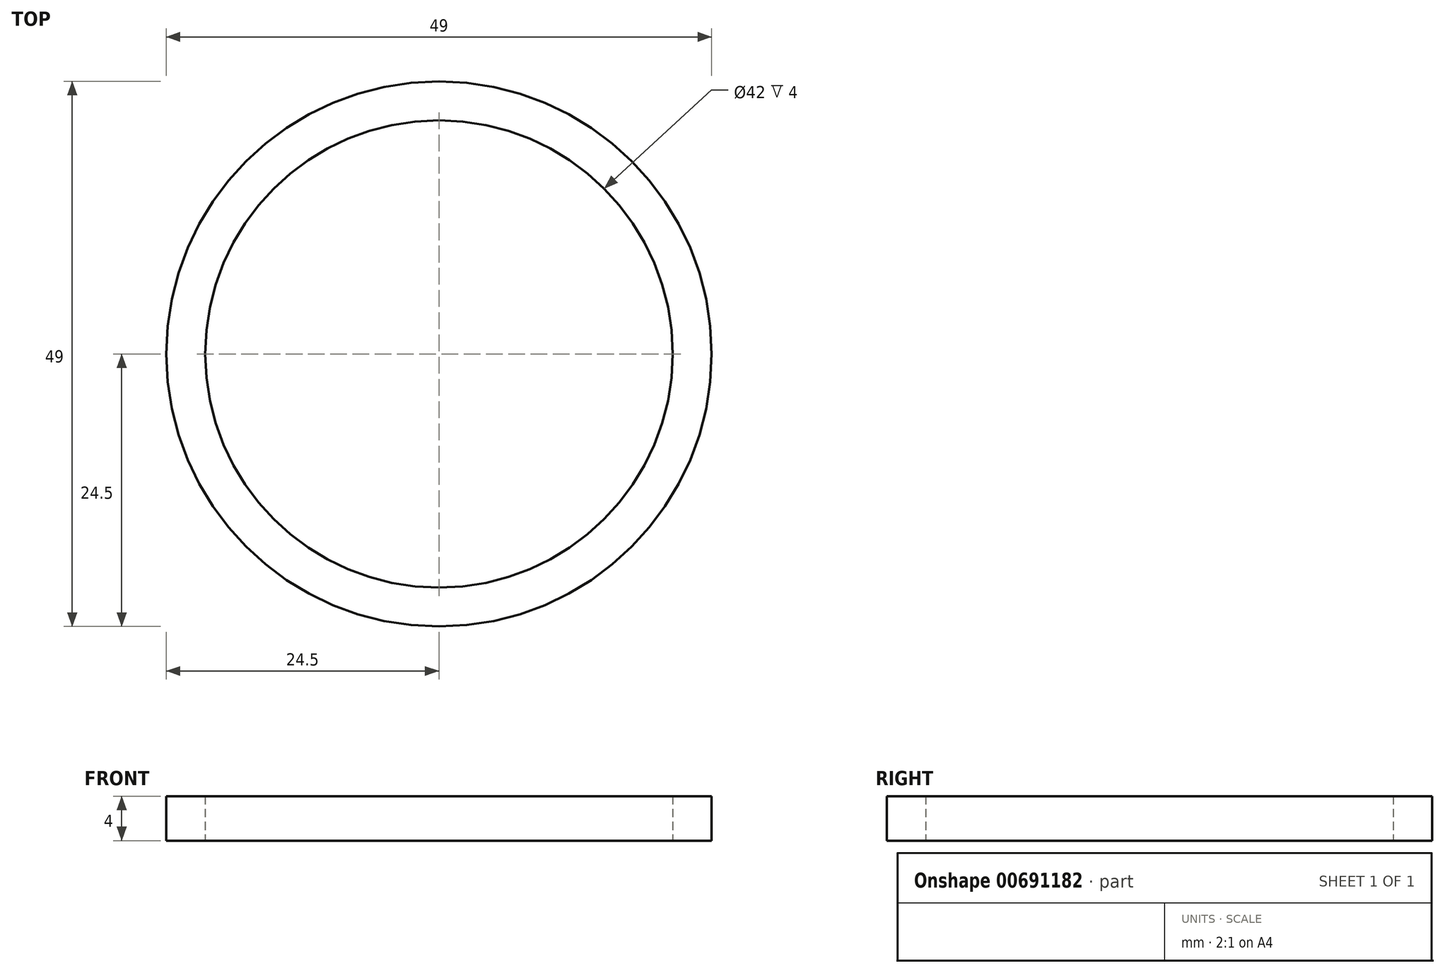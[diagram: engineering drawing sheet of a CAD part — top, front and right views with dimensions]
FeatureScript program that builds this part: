
annotation { "Feature Type Name" : "Feature", "Feature Type Description" : "" }
export const myFeature = defineFeature(function(context is Context, id is Id, definition is map)
    precondition{}
    {
        {
            var Q0;
            Q0=qCreatedBy(makeId("Top.planeOp"),FACE);
            var sketch = newSketch(context, id + "F0", { "sketchPlane" : qUnion([Q0])});
            skCircle(sketch, "E0", {"center": v(0, 0) * mm, "radius": 21 * mm});
            skCircle(sketch, "E1", {"center": v(0, 0) * mm, "radius": 24.5 * mm});
            skSolve(sketch);
        }
        {
            var Q0;
            Q0 = qSketchRegion(id + "F0", true);
            extrude(context, id + "F1", {"entities" : qUnion([Q0]), "depth" : 4 * mm, "offsetDistance" : 25.4 * mm});
        }
    });
